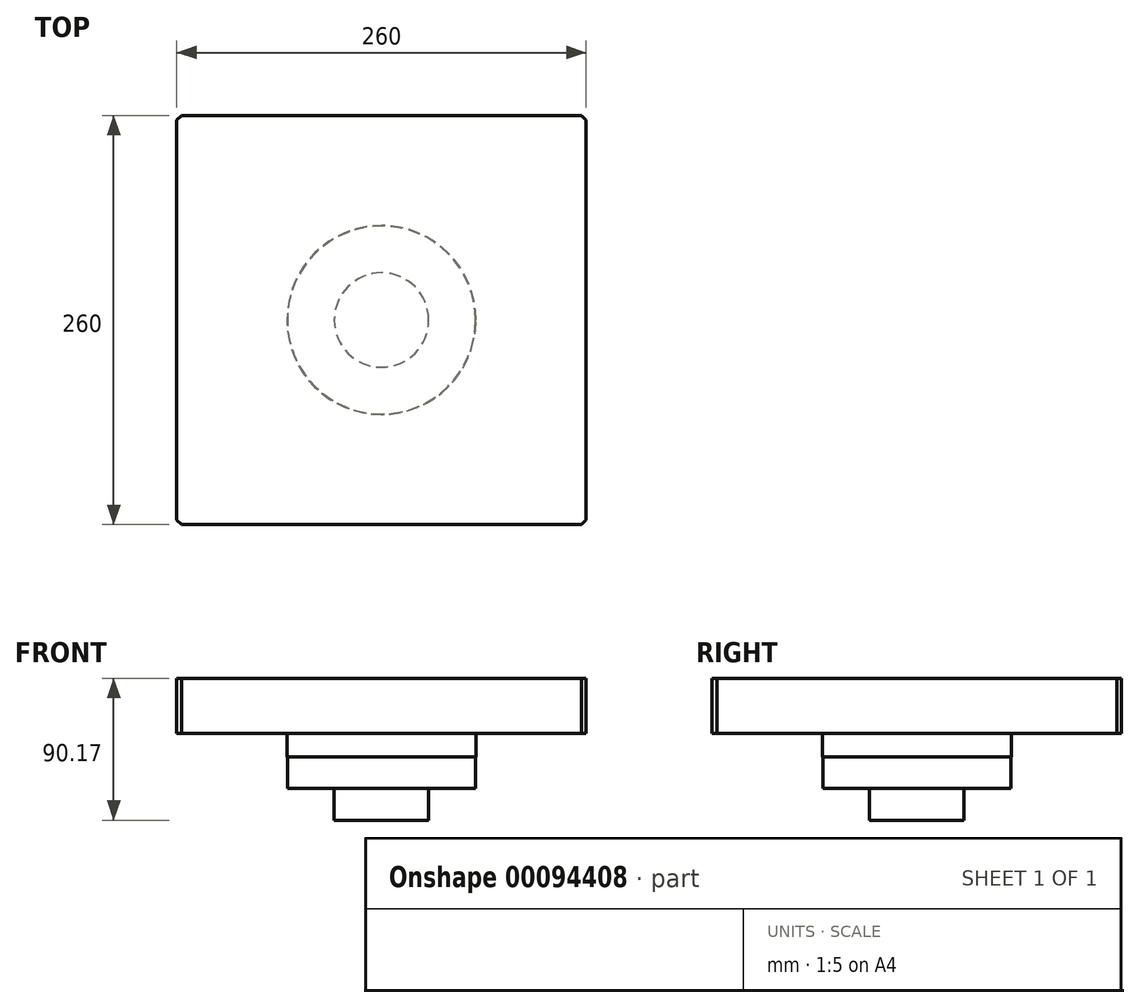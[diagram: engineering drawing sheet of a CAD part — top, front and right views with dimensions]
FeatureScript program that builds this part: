
annotation { "Feature Type Name" : "Feature", "Feature Type Description" : "" }
export const myFeature = defineFeature(function(context is Context, id is Id, definition is map)
    precondition{}
    {
        {
            var Q0;
            Q0=qCreatedBy(makeId("Top.planeOp"),FACE);
            var sketch = newSketch(context, id + "F0", { "sketchPlane" : qUnion([Q0])});
            skLineSegment(sketch, "E0", {"start": v(-142.17, 186.38) * mm, "end": v(117.83, 186.38) * mm});
            skLineSegment(sketch, "E1", {"start": v(-142.17, 186.38) * mm, "end": v(-142.17, -73.62) * mm});
            skLineSegment(sketch, "E2", {"start": v(-142.17, -73.62) * mm, "end": v(117.83, -73.62) * mm});
            skLineSegment(sketch, "E3", {"start": v(117.83, -73.62) * mm, "end": v(117.83, 186.38) * mm});
            skSolve(sketch);
        }
        {
            var Q0;
            Q0=makeQuery(id+"F0.imprint","IMPRINT",FACE,{"disambiguationData":[TD([[makeQuery(id+"F0.imprint","IMPRINT",EDGE,{"derivedFrom":sQuery(id+"F0.wireOp",EDGE,"E0")}),-1.0]])]});
            extrude(context, id + "F1", {"entities" : qUnion([Q0]), "depth" : 35 * mm});
        }
        {
            var Q0;
            Q0=makeQuery(id+"F1.opExtrude","SWEPT_EDGE",EDGE,{"disambiguationData":[OSD([sQuery(id+"F0.wireOp",EDGE,"E2"),sQuery(id+"F0.wireOp",EDGE,"E3")])]});
            var Q1;
            Q1=makeQuery(id+"F1.opExtrude","SWEPT_EDGE",EDGE,{"disambiguationData":[OSD([sQuery(id+"F0.wireOp",EDGE,"E0"),sQuery(id+"F0.wireOp",EDGE,"E3")])]});
            var Q2;
            Q2=makeQuery(id+"F1.opExtrude","SWEPT_EDGE",EDGE,{"disambiguationData":[OSD([sQuery(id+"F0.wireOp",EDGE,"E0"),sQuery(id+"F0.wireOp",EDGE,"E1")])]});
            var Q3;
            Q3=makeQuery(id+"F1.opExtrude","SWEPT_EDGE",EDGE,{"disambiguationData":[OSD([sQuery(id+"F0.wireOp",EDGE,"E1"),sQuery(id+"F0.wireOp",EDGE,"E2")])]});
            chamfer(context, id + "F2", {"entities" : qUnion([Q0, Q1, Q2, Q3]), "width" : 3 * mm, "tangentPropagation" : true});
        }
        {
            var Q0;
            Q0=makeQuery(id+"F1.opExtrude","CAP_FACE",FACE,{"disambiguationData":[OSD([sQuery(id+"F0.wireOp",EDGE,"E0"),sQuery(id+"F0.wireOp",EDGE,"E1"),sQuery(id+"F0.wireOp",EDGE,"E2"),sQuery(id+"F0.wireOp",EDGE,"E3")])],"isStart":true});
            var sketch = newSketch(context, id + "F3", { "sketchPlane" : qUnion([Q0])});
            skCircle(sketch, "E4", {"center": v(-12.17, -56.38) * mm, "radius": 60 * mm});
            skPoint(sketch, "E4.centerSnap0", {"position": v(117.83, -56.38) * mm});
            skPoint(sketch, "E4.centerSnap1", {"position": v(-12.17, -186.38) * mm});
            skSolve(sketch);
        }
        {
            var Q0;
            Q0=makeQuery(id+"F3.imprint","IMPRINT",FACE,{"disambiguationData":[TD([[makeQuery(id+"F3.imprint","IMPRINT",EDGE,{"derivedFrom":sQuery(id+"F3.wireOp",EDGE,"E4")}),1.0]])]});
            extrude(context, id + "F4", {"entities" : qUnion([Q0]), "operationType" : NewBodyOperationType.ADD, "depth" : 15 * mm});
        }
        {
            var Q0;
            Q0=makeQuery(id+"F4.opExtrude","CAP_FACE",FACE,{"disambiguationData":[OSD([sQuery(id+"F3.wireOp",EDGE,"E4")])],"isStart":false});
            var sketch = newSketch(context, id + "F5", { "sketchPlane" : qUnion([Q0])});
            skCircle(sketch, "E5", {"center": v(-12.17, -56.38) * mm, "radius": 59.75 * mm});
            skCircle(sketch, "E6", {"center": v(-12.17, -56.38) * mm, "radius": 30 * mm});
            skCircle(sketch, "E7", {"center": v(-12.17, -56.38) * mm, "radius": 25 * mm});
            skSolve(sketch);
        }
        {
            var Q0;
            Q0=makeQuery(id+"F5.imprint","IMPRINT",FACE,{"disambiguationData":[TD([[makeQuery(id+"F5.imprint","IMPRINT",EDGE,{"derivedFrom":sQuery(id+"F5.wireOp",EDGE,"E5")}),1.0]])]});
            extrude(context, id + "F6", {"entities" : qUnion([Q0]), "operationType" : NewBodyOperationType.ADD, "depth" : 20 * mm});
        }
        {
            var Q0;
            Q0=makeQuery(id+"F6.boolean.opBoolean","SPLIT",FACE,{"disambiguationData":[TD([makeQuery(id+"F6.opExtrude","SWEPT_FACE",FACE,{"disambiguationData":[OSD([sQuery(id+"F5.wireOp",EDGE,"E6")])]})])],"derivedFrom":makeQuery(id+"F4.opExtrude","CAP_FACE",FACE,{"disambiguationData":[OSD([sQuery(id+"F3.wireOp",EDGE,"E4")])],"isStart":false})});
            extrude(context, id + "F7", {"entities" : qUnion([Q0]), "operationType" : NewBodyOperationType.ADD, "depth" : 7 * mm});
        }
        {
            var Q0;
            Q0=makeQuery(id+"F7.opExtrude","CAP_FACE",FACE,{"disambiguationData":[OSD([sQuery(id+"F3.wireOp",EDGE,"E4")])],"isStart":false});
            extrude(context, id + "F8", {"entities" : qUnion([Q0]), "operationType" : NewBodyOperationType.ADD, "depth" : 33.17 * mm});
        }
    });
